# Revit family: ledspotrf-selena-e_7w-dim-930-55d-wh_541003590400
name_source: partatom
category: Lighting Fixtures
units: mm (PartAtom-declared; Revit-internal decimal feet)

## family parameters
Cut with Voids When Loaded = No
Host = Face
Light Source = No
Part Type = Normal
Room Calculation Point = No
Round Connector Dimension = Use Diameter
Shared = No

## types (1)
- LEDSpotRF-Selena-E 7W-DIM-930-55D-WH (1 x LED, 560 lm, 3000)
    Apparent Load = 7 VA
    Approval mark = CE
    CIE Flux Codes = 97 100 100 100 100
    Color Rendering = 90
    Color Temperature = 3000
    Control Gear = Electronic ballast
    Default Elevation = 1800 mm
    Description = Stylish and compact surface mounted spot. Clean “twist-and-lock” mounting system. High quality full metal body. Standard CRI 90.
    Frequency = 60 Hz
    Height = 0 mm  [stored 0 ft]
    Lamp = 1 x LED
    Lamp Light Flux = 560 lm
    Lamp count = 1
    Length = 75 mm
    Luminous efficacy = 80 lm/W
    Manufacturer = OPPLE
    ModVariant = No
    Model = 541003590400
    Mounting Place = Ceiling, Pole
    Mounting Type = Recessed
    Number of Poles = 1
    OnlyDefault = Yes
    Power Factor = 1
    Product Name = LEDSpotRF-Selena-E 7W-DIM-930-55D-WH
    ProductGroupID = 440
    Protection Class = Protection class II
    Protection Degree = IP 20
    RLX_Detail_Level = 1
    RlxData = <blob elided: 133857 chars, md5=e4ed4e67>
    Socket = socket
    Standby Power = 0 W
    System Light Flux = 560 lm
    System Power = 7 W
    Type Comments = Product without accessories
    Type Image = web_selena_rf-7w-wh.jpg
    URL = http://relux.com
    VarID = ---
    Voltage = 230 V
    Voltage Range = 220-240 V
    Weight = 0.00 kg
    Width = 75 mm

note: [stored X ft] marks values corroborated as IEEE doubles in the binary element streams (Revit-internal decimal feet)

## geometry (parser evidence)
native form markers: Blend x4, Sweep x11
no freeform markers — native parametric forms only
